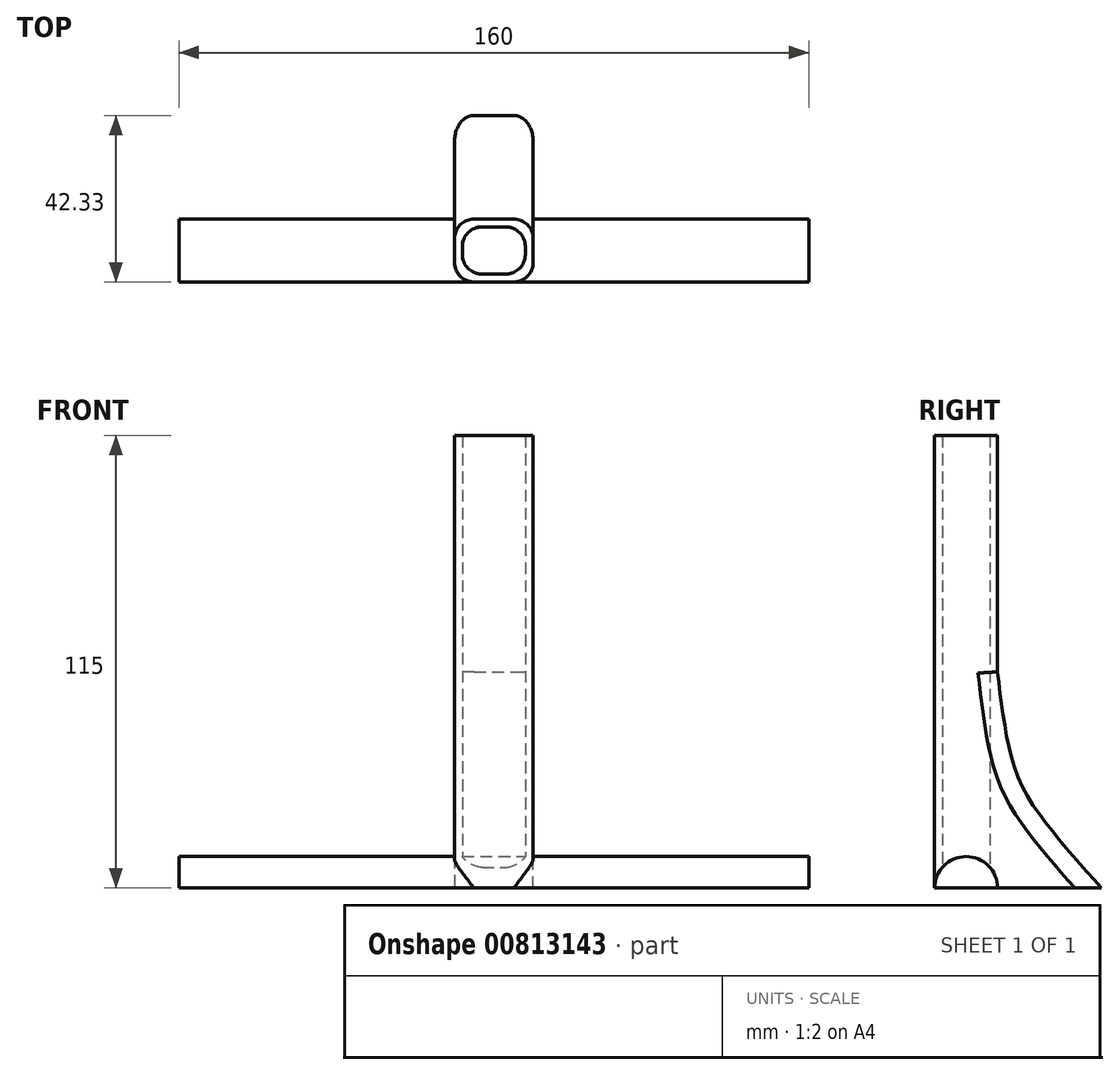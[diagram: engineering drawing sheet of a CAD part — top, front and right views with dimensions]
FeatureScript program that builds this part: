
annotation { "Feature Type Name" : "Feature", "Feature Type Description" : "" }
export const myFeature = defineFeature(function(context is Context, id is Id, definition is map)
    precondition{}
    {
        {
            var Q0;
            Q0=qCreatedBy(makeId("Top.planeOp"),FACE);
            var sketch = newSketch(context, id + "F0", { "sketchPlane" : qUnion([Q0])});
            skLineSegment(sketch, "E0.bottom", {"start": v(-10, 8) * mm, "end": v(10, 8) * mm});
            skLineSegment(sketch, "E0.top", {"start": v(-10, -8) * mm, "end": v(10, -8) * mm});
            skLineSegment(sketch, "E0.left", {"start": v(-10, 8) * mm, "end": v(-10, -8) * mm});
            skLineSegment(sketch, "E0.right", {"start": v(10, 8) * mm, "end": v(10, -8) * mm});
            skSolve(sketch);
        }
        {
            var Q0;
            Q0=makeQuery(id+"F0.imprint","IMPRINT",FACE,{"disambiguationData":[TD([[makeQuery(id+"F0.imprint","IMPRINT",EDGE,{"derivedFrom":sQuery(id+"F0.wireOp",EDGE,"E0.bottom")}),-1.0]])]});
            extrude(context, id + "F1", {"entities" : qUnion([Q0]), "depth" : 100 * mm, "offsetDistance" : 25 * mm, "hasSecondDirection" : true, "secondDirectionOppositeDirection" : true, "secondDirectionDepth" : 15 * mm});
        }
        {
            var Q0;
            Q0=makeQuery(id+"F1.opExtrude","CAP_FACE",FACE,{"disambiguationData":[OSD([sQuery(id+"F0.wireOp",EDGE,"E0.bottom"),sQuery(id+"F0.wireOp",EDGE,"E0.top"),sQuery(id+"F0.wireOp",EDGE,"E0.left"),sQuery(id+"F0.wireOp",EDGE,"E0.right")])],"isStart":false});
            shell(context, id + "F2", {"entities" : qUnion([Q0]), "thickness" : 2 * mm});
        }
        {
            var Q0;
            Q0=qCreatedBy(makeId("Top.planeOp"),FACE);
            var sketch = newSketch(context, id + "F3", { "sketchPlane" : qUnion([Q0])});
            skCircle(sketch, "E1", {"center": v(-23, 31) * mm, "radius": 6.65 * mm});
            skSolve(sketch);
        }
        {
            var Q0;
            Q0 = qSketchRegion(id + "F3", true);
            extrude(context, id + "F4", {"entities" : qUnion([Q0]), "operationType" : NewBodyOperationType.REMOVE, "depth" : 25 * mm, "offsetDistance" : 25 * mm});
        }
        {
            var Q0;
            Q0=makeQuery(id+"FCLa9WVoEjQcUB1_1.boolean.opBoolean","MERGE",FACE,{"derivedFrom":[makeQuery(id+"F1.opExtrude","SWEPT_FACE",FACE,{"disambiguationData":[OSD([sQuery(id+"F0.wireOp",EDGE,"E0.right")])]}),makeQuery(id+"FCLa9WVoEjQcUB1_1.opExtrude","CAP_FACE",FACE,{"disambiguationData":[OSD([sQuery(id+"FcnMVS3fHe6Ncpx_1.wireOp",EDGE,"fd3b3ce7-7962-4191-a88d-5f3231b83800"),sQuery(id+"FcnMVS3fHe6Ncpx_1.wireOp",EDGE,"Zq7ENsFC-tDQg-VSh3-AuBV-LEuFHlCRDXwB"),sQuery(id+"FcnMVS3fHe6Ncpx_1.wireOp",EDGE,"FNIUXcVH-CpcB-eava-yW9A-poUxp1CqerXA")])],"isStart":false})]});
            var sketch = newSketch(context, id + "F5", { "sketchPlane" : qUnion([Q0])});
            skArc(sketch, "E2", {"start": v(8, -15) * mm, "mid": v(0, -7) * mm, "end": v(-8, -15) * mm});
            skLineSegment(sketch, "E3", {"start": v(8, -15) * mm, "end": v(-8, -15) * mm});
            skSolve(sketch);
        }
        {
            var Q0;
            Q0=makeQuery(id+"F1.opExtrude","CAP_FACE",FACE,{"disambiguationData":[OSD([sQuery(id+"F0.wireOp",EDGE,"E0.bottom"),sQuery(id+"F0.wireOp",EDGE,"E0.top"),sQuery(id+"F0.wireOp",EDGE,"E0.left"),sQuery(id+"F0.wireOp",EDGE,"E0.right")])],"isStart":true});
            var sketch = newSketch(context, id + "F6", { "sketchPlane" : qUnion([Q0])});
            skLineSegment(sketch, "E4", {"start": v(-80, 0) * mm, "end": v(80, 0) * mm});
            skSolve(sketch);
        }
        {
            var Q0;
            Q0=makeQuery(id+"F5.imprint","IMPRINT",FACE,{"disambiguationData":[TD([[makeQuery(id+"F5.imprint","IMPRINT",EDGE,{"derivedFrom":sQuery(id+"F5.wireOp",EDGE,"E2")}),1.0]])]});
            var Q1;
            Q1=sQuery(id+"F6.wireOp",EDGE,"E4");
            sweep(context, id + "F7", {"operationType" : NewBodyOperationType.ADD, "profiles" : qUnion([Q0]), "path" : qUnion([Q1])});
        }
        {
            var Q0;
            Q0=makeQuery(id+"F1.opExtrude","SWEPT_FACE",FACE,{"disambiguationData":[OSD([sQuery(id+"F0.wireOp",EDGE,"E0.right")])]});
            var sketch = newSketch(context, id + "F8", { "sketchPlane" : qUnion([Q0])});
            skLineSegment(sketch, "E5", {"start": v(7.51, -15) * mm, "end": v(7.51, 44.31) * mm});
            skFitSpline(sketch, "E6", {"points": [v(7.51, 44.31) * mm, v(11.5, 18.16) * mm, v(17.8, 4.88) * mm, v(34.33, -15) * mm], "startDerivative": vector(8.75, -78.75) * mm, "endDerivative": vector(51.72, -58.3) * mm});
            skLineSegment(sketch, "E7", {"start": v(7.51, -15) * mm, "end": v(34.33, -15) * mm});
            skSolve(sketch);
        }
        {
            var Q0;
            {var subQ0=sQuery(id+"F8.wireOp",EDGE,"E7");var subQ1=sQuery(id+"F8.wireOp",EDGE,"E6");var subQ2=makeQuery(id+"F8.imprint","INTERSECT",VERTEX,{"derivedFrom":[subQ1,subQ0]});Q0=makeQuery(id+"F8.imprint","IMPRINT",FACE,{"disambiguationData":[TD([[makeQuery(id+"F8.imprint","IMPRINT",EDGE,{"disambiguationData":[TD([[subQ2,1.0]])],"derivedFrom":subQ1}),-1.0]])]});}
            extrude(context, id + "F9", {"entities" : qUnion([Q0]), "operationType" : NewBodyOperationType.ADD, "oppositeDirection" : true, "depth" : 20 * mm, "offsetDistance" : 25 * mm});
        }
        {
            var Q0;
            Q0=makeQuery(id+"F2.opShell","OFFSET_EDGE",EDGE,{"disambiguationData":[OSD([sQuery(id+"F0.wireOp",EDGE,"E0.top"),sQuery(id+"F0.wireOp",EDGE,"E0.left")])]});
            var Q1;
            Q1=makeQuery(id+"F2.opShell","OFFSET_EDGE",EDGE,{"disambiguationData":[OSD([sQuery(id+"F0.wireOp",EDGE,"E0.top"),sQuery(id+"F0.wireOp",EDGE,"E0.right")])]});
            var Q2;
            Q2=makeQuery(id+"F1.opExtrude","SWEPT_EDGE",EDGE,{"disambiguationData":[OSD([sQuery(id+"F0.wireOp",EDGE,"E0.top"),sQuery(id+"F0.wireOp",EDGE,"E0.right")])]});
            var Q3;
            Q3=makeQuery(id+"F1.opExtrude","SWEPT_EDGE",EDGE,{"disambiguationData":[OSD([sQuery(id+"F0.wireOp",EDGE,"E0.top"),sQuery(id+"F0.wireOp",EDGE,"E0.left")])]});
            var Q4;
            Q4=makeQuery(id+"F2.opShell","OFFSET_EDGE",EDGE,{"disambiguationData":[OSD([sQuery(id+"F0.wireOp",EDGE,"E0.bottom"),sQuery(id+"F0.wireOp",EDGE,"E0.right")])]});
            var Q5;
            Q5=makeQuery(id+"F2.opShell","OFFSET_EDGE",EDGE,{"disambiguationData":[OSD([sQuery(id+"F0.wireOp",EDGE,"E0.bottom"),sQuery(id+"F0.wireOp",EDGE,"E0.left")])]});
            var Q6;
            Q6=makeQuery(id+"F1.opExtrude","SWEPT_EDGE",EDGE,{"disambiguationData":[OSD([sQuery(id+"F0.wireOp",EDGE,"E0.bottom"),sQuery(id+"F0.wireOp",EDGE,"E0.right")])]});
            var Q7;
            Q7=makeQuery(id+"F1.opExtrude","SWEPT_EDGE",EDGE,{"disambiguationData":[OSD([sQuery(id+"F0.wireOp",EDGE,"E0.bottom"),sQuery(id+"F0.wireOp",EDGE,"E0.left")])]});
            var Q8;
            Q8=makeQuery(id+"F9.opExtrude","CAP_EDGE",EDGE,{"disambiguationData":[OSD([sQuery(id+"F8.wireOp",EDGE,"E6")])],"isStart":true});
            var Q9;
            Q9=makeQuery(id+"F9.opExtrude","CAP_EDGE",EDGE,{"disambiguationData":[OSD([sQuery(id+"F8.wireOp",EDGE,"E6")])],"isStart":false});
            fillet(context, id + "F10", {"entities" : qUnion([Q0, Q1, Q2, Q3, Q4, Q5, Q6, Q7, Q8, Q9]), "radius" : 5 * mm, "tangentPropagation" : true, "allowEdgeOverflow" : false});
        }
    });
